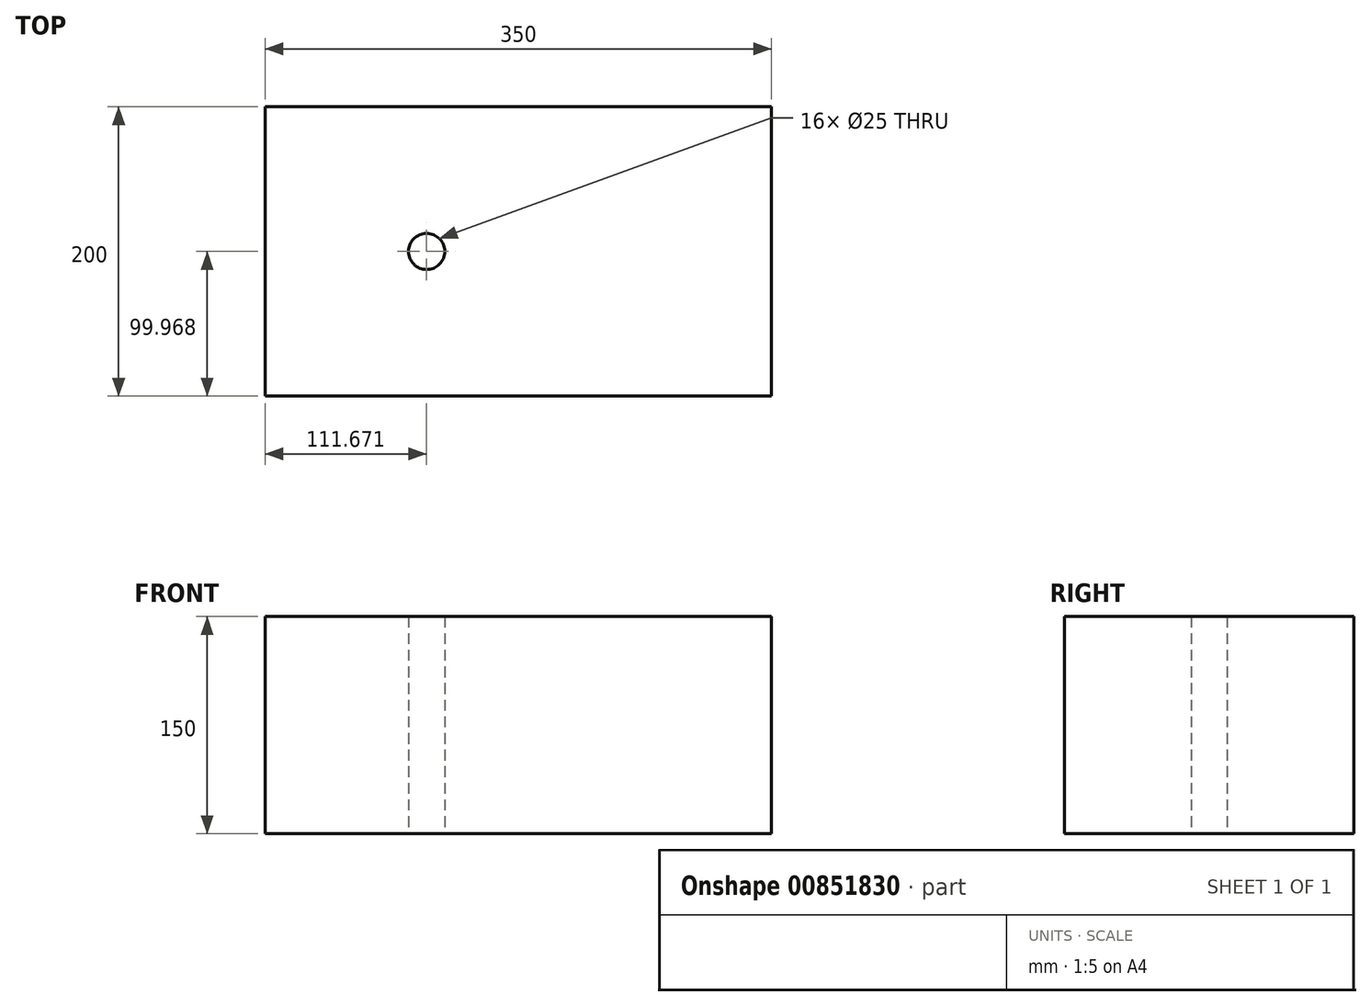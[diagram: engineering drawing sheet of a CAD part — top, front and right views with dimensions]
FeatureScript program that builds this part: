
annotation { "Feature Type Name" : "Feature", "Feature Type Description" : "" }
export const myFeature = defineFeature(function(context is Context, id is Id, definition is map)
    precondition{}
    {
        {
            var Q0;
            Q0=qCreatedBy(makeId("Top.planeOp"),FACE);
            var sketch = newSketch(context, id + "F0", { "sketchPlane" : qUnion([Q0])});
            skLineSegment(sketch, "E0.bottom", {"start": v(175, -100) * mm, "end": v(-175, -100) * mm});
            skLineSegment(sketch, "E0.top", {"start": v(175, 100) * mm, "end": v(-175, 100) * mm});
            skLineSegment(sketch, "E0.left", {"start": v(175, -100) * mm, "end": v(175, 100) * mm});
            skLineSegment(sketch, "E0.right", {"start": v(-175, -100) * mm, "end": v(-175, 100) * mm});
            skPoint(sketch, "E0.middle", {"position": v(0, 0) * mm});
            skLineSegment(sketch, "E1", {"start": v(0, 100) * mm, "end": v(0, -100) * mm, "construction": true});
            skLineSegment(sketch, "E2", {"start": v(-175, 0) * mm, "end": v(175, 0) * mm, "construction": true});
            skPoint(sketch, "E3.middle", {"position": v(-63.33, -0.03) * mm});
            skCircle(sketch, "E4", {"center": v(-63.33, -0.03) * mm, "radius": 12.5 * mm});
            skSolve(sketch);
        }
        {
            var Q0;
            Q0=makeQuery(id+"F0.imprint","IMPRINT",FACE,{"disambiguationData":[TD([[makeQuery(id+"F0.imprint","IMPRINT",EDGE,{"derivedFrom":sQuery(id+"F0.wireOp",EDGE,"E0.bottom")}),-1.0]])]});
            extrude(context, id + "F1", {"entities" : qUnion([Q0]), "depth" : 150 * mm, "offsetDistance" : 25 * mm});
        }
    });
